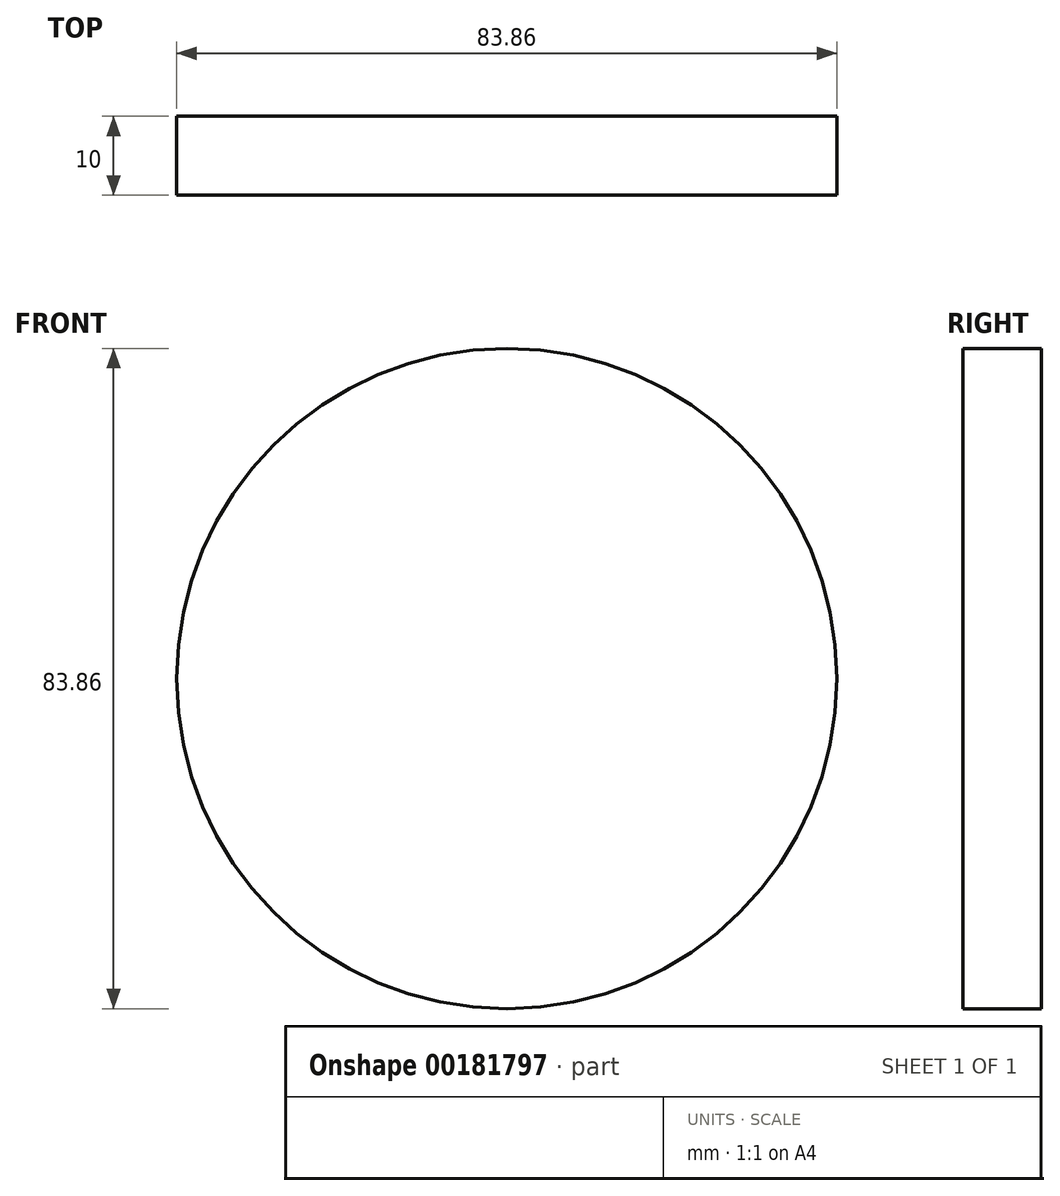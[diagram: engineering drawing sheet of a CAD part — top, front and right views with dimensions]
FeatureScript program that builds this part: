
annotation { "Feature Type Name" : "Feature", "Feature Type Description" : "" }
export const myFeature = defineFeature(function(context is Context, id is Id, definition is map)
    precondition{}
    {
        {
            var Q0;
            Q0=qCreatedBy(makeId("Front.planeOp"),FACE);
            var sketch = newSketch(context, id + "F0", { "sketchPlane" : qUnion([Q0])});
            skCircle(sketch, "E0", {"center": v(0, 0) * mm, "radius": 41.93 * mm});
            skSolve(sketch);
        }
        {
            var Q0;
            Q0=makeQuery(id+"F0.imprint","IMPRINT",FACE,{"disambiguationData":[TD([[makeQuery(id+"F0.imprint","IMPRINT",EDGE,{"derivedFrom":sQuery(id+"F0.wireOp",EDGE,"E0")}),1.0]])]});
            extrude(context, id + "F1", {"entities" : qUnion([Q0]), "depth" : 10 * mm});
        }
    });
